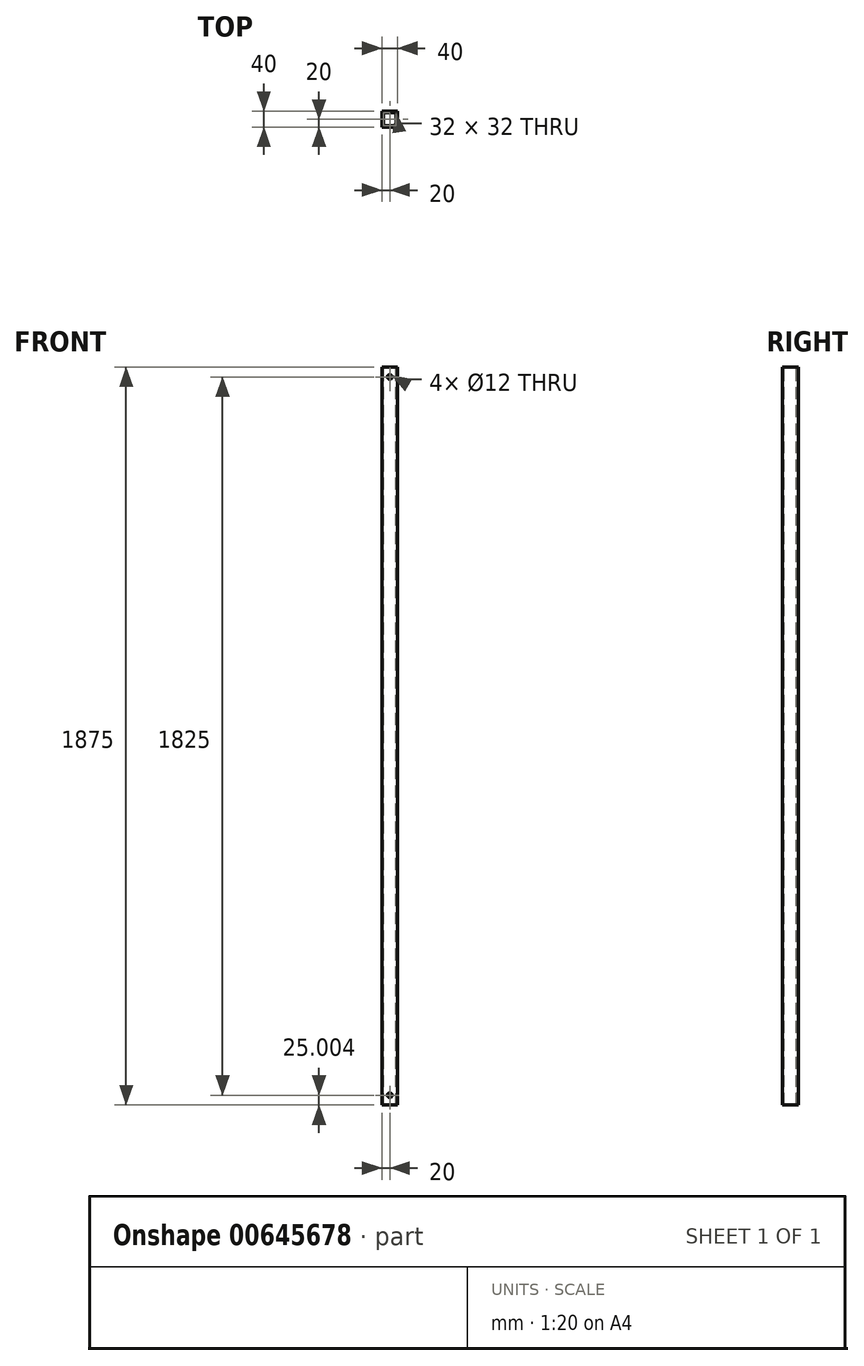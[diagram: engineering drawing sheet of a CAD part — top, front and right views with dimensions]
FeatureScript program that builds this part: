
annotation { "Feature Type Name" : "Feature", "Feature Type Description" : "" }
export const myFeature = defineFeature(function(context is Context, id is Id, definition is map)
    precondition{}
    {
        {
            var Q0;
            Q0=qCreatedBy(makeId("Front.planeOp"),FACE);
            var sketch = newSketch(context, id + "F0", { "sketchPlane" : qUnion([Q0])});
            skLineSegment(sketch, "E0.bottom", {"start": v(0, -9.75) * mm, "end": v(40, -9.75) * mm});
            skLineSegment(sketch, "E0.top", {"start": v(0, 1865.25) * mm, "end": v(40, 1865.25) * mm});
            skLineSegment(sketch, "E0.left", {"start": v(0, -9.75) * mm, "end": v(0, 1865.25) * mm});
            skLineSegment(sketch, "E0.right", {"start": v(40, -9.75) * mm, "end": v(40, 1865.25) * mm});
            skLineSegment(sketch, "E1", {"start": v(20, -9.75) * mm, "end": v(20, 1865.25) * mm, "construction": true});
            skCircle(sketch, "E2", {"center": v(20, 15.25) * mm, "radius": 6 * mm});
            skCircle(sketch, "E3", {"center": v(20, 1840.25) * mm, "radius": 6 * mm});
            skSolve(sketch);
        }
        {
            var Q0;
            Q0 = qSketchRegion(id + "F0", true);
            extrude(context, id + "F1", {"entities" : qUnion([Q0]), "depth" : 40 * mm, "offsetDistance" : 25 * mm});
        }
        {
            var Q0;
            Q0=makeQuery(id+"F1.opExtrude","SWEPT_FACE",FACE,{"disambiguationData":[OSD([sQuery(id+"F0.wireOp",EDGE,"E0.top")])]});
            var sketch = newSketch(context, id + "F2", { "sketchPlane" : qUnion([Q0])});
            skPoint(sketch, "E4.firstSnap0", {"position": v(4, -40) * mm});
            skLineSegment(sketch, "E4.bottom", {"start": v(4, -4) * mm, "end": v(36, -4) * mm});
            skLineSegment(sketch, "E4.top", {"start": v(4, -36) * mm, "end": v(36, -36) * mm});
            skLineSegment(sketch, "E4.left", {"start": v(4, -4) * mm, "end": v(4, -36) * mm});
            skLineSegment(sketch, "E4.right", {"start": v(36, -4) * mm, "end": v(36, -36) * mm});
            skSolve(sketch);
        }
        {
            var Q0;
            Q0 = qSketchRegion(id + "F2", true);
            extrude(context, id + "F3", {"entities" : qUnion([Q0]), "operationType" : NewBodyOperationType.REMOVE, "endBound" : BoundingType.THROUGH_ALL, "oppositeDirection" : true, "depth" : 25 * mm, "offsetDistance" : 25 * mm});
        }
    });
